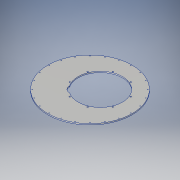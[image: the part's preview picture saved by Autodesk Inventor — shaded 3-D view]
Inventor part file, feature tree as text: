
AUTODESK INVENTOR PART (.ipt)
format: ipt  version: 2018 (Build 220112000, 112)  size: 171,008 bytes
history: native  units: in
note: dims shown in document units (in); Inventor stores cm internally (conversion verified against a paired STEP export)
features: sketch x5, extrude x3, hole x2, pattern_circular x2
ambient origin geometry x8: Origin, YZ Plane, XZ Plane, XY Plane, X Axis, Y Axis, Z Axis, Center Point
bodies: Solid1 (feature_tree)
feature tree (12):
  extrude  "Extrusion1"  Depth=0.25in TaperAngle=0.0deg
  hole  "Hole3"  [1 undecoded]
  pattern_circular  "Circular Pattern1"  [2 undecoded]
  extrude  "Extrusion4"  Depth=0.25in TaperAngle=0.0deg
  hole  "Hole4"  [1 undecoded]
  pattern_circular  "Circular Pattern2"  Angle=22.5deg  [1 undecoded]
  extrude  "Extrusion5"  Depth=0.25in TaperAngle=360.0deg
  sketch  "Sketch1"  dims[d0=18.0in d1=0.25in d2=0.0in]
  sketch  "Sketch7"  dims[d42=8.75in]
  sketch  "Sketch8"  dims[d43=0.13in d44=0.328in d45=0.375in d46=0.25in d47=0.5635in d48=0.484in d49=0.8108in d50=9.4488in d51=360.0deg]
  sketch  "Sketch9"  dims[d53=1.56in]
  sketch  "Sketch10"  dims[d54=45.0deg d55=9.5in d56=1.0in d57=0.0in d58=5.0in d59=22.5deg d60=0.266in d61=0.5in d62=0.507in d63=0.25in d64=0.5635in d65=1.0in d66=0.8108in d67=3.1496in d68=360.0deg d70=2.25in d71=135.0deg d72=2.5in d73=1.0in d74=0.0in]
note: 5 required parameter values undecoded (feature->parameter linkage not recoverable at this tier; creation-order binding heuristic only, values carry confidence <= 0.55)
